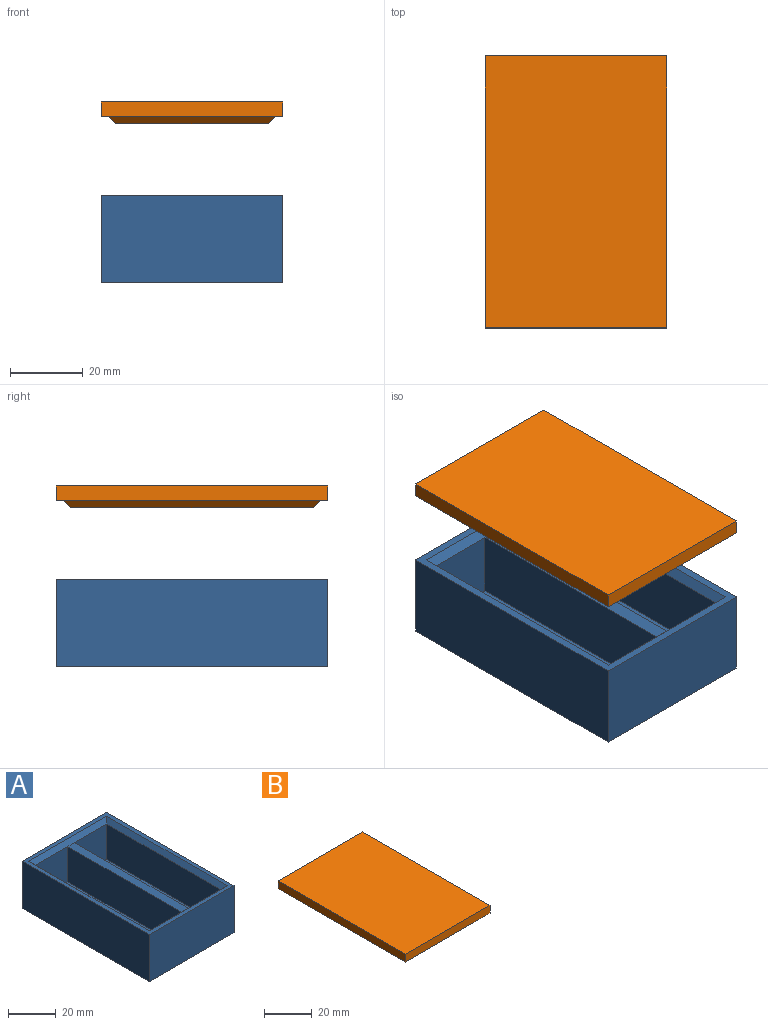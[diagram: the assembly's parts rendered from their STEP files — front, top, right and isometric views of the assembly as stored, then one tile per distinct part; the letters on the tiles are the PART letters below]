
ASSEMBLY  parts=2 mates=1
PART A: 21 faces, bbox 50x75x24 mm
  f0: plane 19x18mm, normal (0,1,0), area 342mm2, adj f4,f12,f16,f20
  f1: plane 19x18mm, normal (0,-1,0), area 342mm2, adj f4,f12,f15,f20
  f2: plane 19x18mm, normal (0,1,0), area 342mm2, adj f9,f13,f16,f19
  f3: plane 19x18mm, normal (0,-1,0), area 342mm2, adj f9,f13,f15,f19
  f4: plane 67x18mm, normal (-1,0,0), area 1206mm2, adj f0,f1,f12,f17
  f5: plane 75x24mm, normal (1,0,0), area 1800mm2, adj f6,f8,f10,f11
  f6: plane 50x24mm, normal (0,1,0), area 1200mm2, adj f5,f7,f10,f11
  f7: plane 75x24mm, normal (-1,0,0), area 1800mm2, adj f6,f8,f10,f11
  f8: plane 50x24mm, normal (0,-1,0), area 1200mm2, adj f5,f7,f10,f11
  f9: plane 67x18mm, normal (1,0,0), area 1206mm2, adj f2,f3,f13,f14
  f10: plane 75x50mm, normal (0,0,1), area 484mm2, adj f5,f6,f7,f8,f14,f15,f16,f17
  f11: plane 75x50mm, normal (0,0,-1), area 3750mm2, adj f5,f6,f7,f8
  f12: plane 67x19mm, normal (0,0,1), area 1273mm2, adj f0,f1,f4,f20
  f13: plane 67x19mm, normal (0,0,1), area 1273mm2, adj f2,f3,f9,f19
  f14: plane 71x2mm, normal (0.71,0,0.71), area 195.2mm2, adj f9,f10,f15,f16
  f15: plane 46x2mm, normal (0,-0.71,0.71), area 124.5mm2, adj f1,f3,f10,f14,f17,f18
  f16: plane 46x2mm, normal (0,0.71,0.71), area 124.5mm2, adj f0,f2,f10,f14,f17,f18
  f17: plane 71x2mm, normal (-0.71,0,0.71), area 195.2mm2, adj f4,f10,f15,f16
  f18: plane 67x4mm, normal (0,0,1), area 268mm2, adj f15,f16,f19,f20
  f19: plane 67x18mm, normal (-1,0,0), area 1206mm2, adj f2,f3,f13,f18
  f20: plane 67x18mm, normal (1,0,0), area 1206mm2, adj f0,f1,f12,f18
PART B: 11 faces, bbox 50x75x6 mm
  f0: plane 75x4mm, normal (-1,0,0), area 300mm2, adj f1,f3,f4,f5
  f1: plane 50x4mm, normal (0,-1,0), area 200mm2, adj f0,f2,f4,f5
  f2: plane 75x4mm, normal (1,0,0), area 300mm2, adj f1,f3,f4,f5
  f3: plane 50x4mm, normal (0,1,0), area 200mm2, adj f0,f2,f4,f5
  f4: plane 75x50mm, normal (0,0,-1), area 484mm2, adj f0,f1,f2,f3,f7,f8,f9,f10
  f5: plane 75x50mm, normal (0,0,1), area 3750mm2, adj f0,f1,f2,f3
  f6: plane 67x42mm, normal (0,0,-1), area 2814mm2, adj f7,f8,f9,f10
  f7: plane 71x2mm, normal (-0.71,0,-0.71), area 195.2mm2, adj f4,f6,f8,f9
  f8: plane 46x2mm, normal (0,-0.71,-0.71), area 124.5mm2, adj f4,f6,f7,f10
  f9: plane 46x2mm, normal (0,0.71,-0.71), area 124.5mm2, adj f4,f6,f7,f10
  f10: plane 71x2mm, normal (0.71,0,-0.71), area 195.2mm2, adj f4,f6,f8,f9
PLACE A t=(-16.45,-23.54,-17.76)mm
PLACE B t=(-16.45,-23.54,31.9)mm
MATE slider B.f6 <-> A.f18  axis (0,0,-1) through (-16.45,-23.54,25.9)mm
